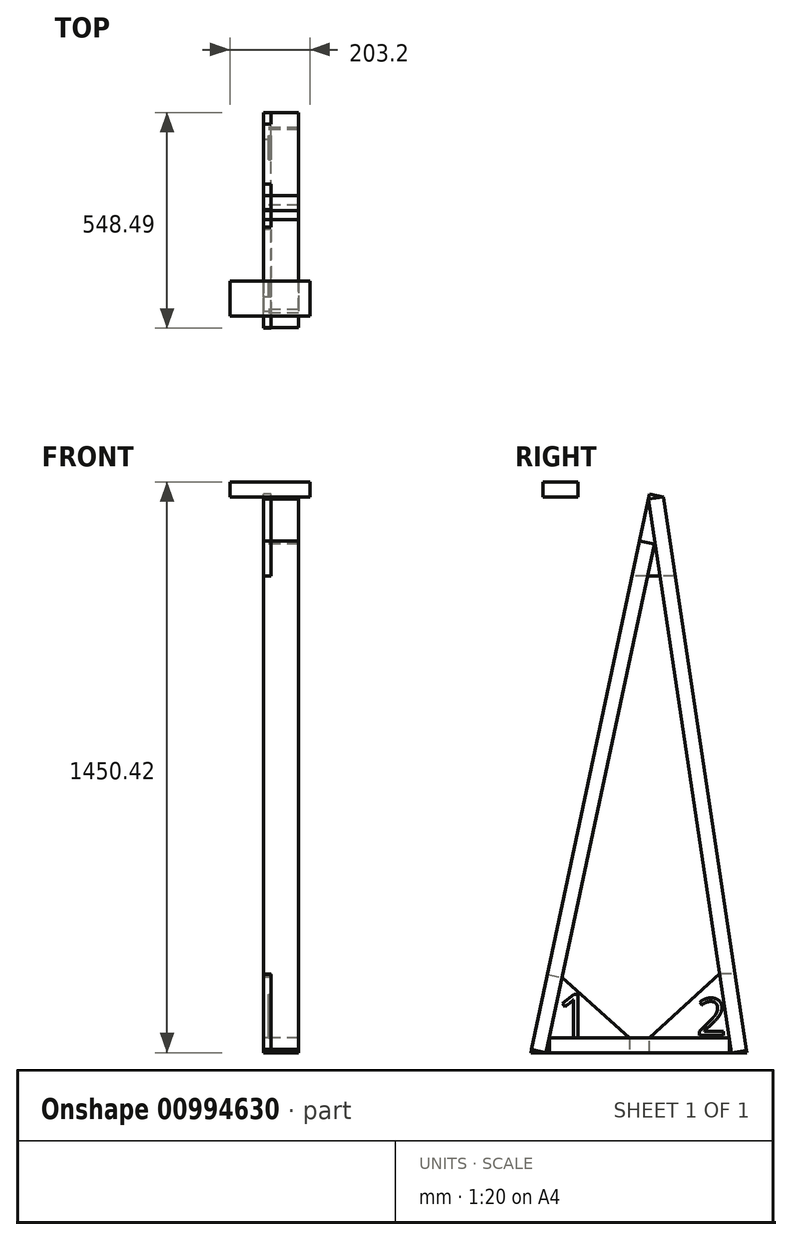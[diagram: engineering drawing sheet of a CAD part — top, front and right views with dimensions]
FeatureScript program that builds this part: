
annotation { "Feature Type Name" : "Feature", "Feature Type Description" : "" }
export const myFeature = defineFeature(function(context is Context, id is Id, definition is map)
    precondition{}
    {
        {
            var Q0;
            Q0=qCreatedBy(makeId("Right.planeOp"),FACE);
            var sketch = newSketch(context, id + "F0", { "sketchPlane" : qUnion([Q0])});
            skLineSegment(sketch, "E0.bottom", {"start": v(-72.85, 56) * mm, "end": v(384.35, 56) * mm});
            skLineSegment(sketch, "E0.top", {"start": v(-72.85, 17.9) * mm, "end": v(384.35, 17.9) * mm});
            skLineSegment(sketch, "E0.left", {"start": v(-72.85, 56) * mm, "end": v(-72.85, 17.9) * mm});
            skLineSegment(sketch, "E0.right", {"start": v(384.35, 56) * mm, "end": v(384.35, 17.9) * mm});
            skSolve(sketch);
        }
        {
            var Q0;
            Q0=makeQuery(id+"F0.imprint","IMPRINT",FACE,{"disambiguationData":[TD([[makeQuery(id+"F0.imprint","IMPRINT",EDGE,{"derivedFrom":sQuery(id+"F0.wireOp",EDGE,"E0.bottom")}),-1.0]])]});
            extrude(context, id + "F1", {"entities" : qUnion([Q0]), "depth" : 88.9 * mm, "offsetDistance" : 25.4 * mm});
        }
        {
            var Q0;
            Q0=qCreatedBy(makeId("Right.planeOp"),FACE);
            var sketch = newSketch(context, id + "F2", { "sketchPlane" : qUnion([Q0])});
            skLineSegment(sketch, "E1.bottom", {"start": v(156.4, 1317.77) * mm, "end": v(193.66, 1309.84) * mm});
            skLineSegment(sketch, "E1.top", {"start": v(-118.22, 25.83) * mm, "end": v(-80.95, 17.9) * mm});
            skLineSegment(sketch, "E1.left", {"start": v(156.4, 1317.77) * mm, "end": v(-118.22, 25.83) * mm});
            skLineSegment(sketch, "E1.right", {"start": v(193.66, 1309.84) * mm, "end": v(-80.95, 17.9) * mm});
            skSolve(sketch);
        }
        {
            var Q0;
            Q0=makeQuery(id+"F2.imprint","IMPRINT",FACE,{"disambiguationData":[TD([[makeQuery(id+"F2.imprint","IMPRINT",EDGE,{"derivedFrom":sQuery(id+"F2.wireOp",EDGE,"E1.bottom")}),-1.0]])]});
            extrude(context, id + "F3", {"entities" : qUnion([Q0]), "depth" : 88.9 * mm, "offsetDistance" : 25.4 * mm});
        }
        {
            var Q0;
            Q0=qCreatedBy(makeId("Right.planeOp"),FACE);
            var sketch = newSketch(context, id + "F4", { "sketchPlane" : qUnion([Q0])});
            skLineSegment(sketch, "E2.bottom", {"start": v(179.1, 1424.58) * mm, "end": v(216.77, 1430.23) * mm});
            skLineSegment(sketch, "E2.top", {"start": v(390.06, 17.9) * mm, "end": v(427.74, 23.56) * mm});
            skLineSegment(sketch, "E2.left", {"start": v(179.1, 1424.58) * mm, "end": v(390.06, 17.9) * mm});
            skLineSegment(sketch, "E2.right", {"start": v(216.77, 1430.23) * mm, "end": v(427.74, 23.56) * mm});
            skSolve(sketch);
        }
        {
            var Q0;
            Q0=makeQuery(id+"F4.imprint","IMPRINT",FACE,{"disambiguationData":[TD([[makeQuery(id+"F4.imprint","IMPRINT",EDGE,{"derivedFrom":sQuery(id+"F4.wireOp",EDGE,"E2.bottom")}),-1.0]])]});
            extrude(context, id + "F5", {"entities" : qUnion([Q0]), "depth" : 88.9 * mm, "offsetDistance" : 25.4 * mm});
        }
        {
            var Q0;
            Q0=qCreatedBy(makeId("Front.planeOp"),FACE);
            var sketch = newSketch(context, id + "F6", { "sketchPlane" : qUnion([Q0])});
            skLineSegment(sketch, "E3.bottom", {"start": v(-85.7, 1468.33) * mm, "end": v(117.5, 1468.33) * mm});
            skLineSegment(sketch, "E3.top", {"start": v(-85.7, 1430.23) * mm, "end": v(117.5, 1430.23) * mm});
            skLineSegment(sketch, "E3.left", {"start": v(-85.7, 1468.33) * mm, "end": v(-85.7, 1430.23) * mm});
            skLineSegment(sketch, "E3.right", {"start": v(117.5, 1468.33) * mm, "end": v(117.5, 1430.23) * mm});
            skSolve(sketch);
        }
        {
            var Q0;
            Q0=makeQuery(id+"F6.imprint","IMPRINT",FACE,{"disambiguationData":[TD([[makeQuery(id+"F6.imprint","IMPRINT",EDGE,{"derivedFrom":sQuery(id+"F6.wireOp",EDGE,"E3.bottom")}),-1.0]])]});
            extrude(context, id + "F7", {"entities" : qUnion([Q0]), "depth" : 88.9 * mm, "offsetDistance" : 25.4 * mm});
        }
        {
            var Q0;
            Q0=qCreatedBy(makeId("Right.planeOp"),FACE);
            var sketch = newSketch(context, id + "F8", { "sketchPlane" : qUnion([Q0])});
            skLineSegment(sketch, "E4", {"start": v(-119.9, 17.9) * mm, "end": v(-77.65, 216.67) * mm});
            skLineSegment(sketch, "E5", {"start": v(-77.65, 216.67) * mm, "end": v(-40.39, 208.75) * mm});
            skLineSegment(sketch, "E6", {"start": v(-40.39, 208.75) * mm, "end": v(130.35, 56) * mm});
            skLineSegment(sketch, "E7", {"start": v(130.35, 56) * mm, "end": v(130.35, 17.9) * mm});
            skLineSegment(sketch, "E8", {"start": v(130.35, 17.9) * mm, "end": v(-119.9, 17.9) * mm});
            skSolve(sketch);
        }
        {
            var Q0;
            Q0=qSketchRegion(id+"F8",true);
            extrude(context, id + "F9", {"entities" : qUnion([Q0]), "depth" : 19.05 * mm, "offsetDistance" : 25.4 * mm});
        }
        {
            var Q0;
            Q0=makeQuery(id+"F9.opExtrude","CAP_FACE",FACE,{"disambiguationData":[OSD([sQuery(id+"F8.wireOp",EDGE,"E4"),sQuery(id+"F8.wireOp",EDGE,"E5"),sQuery(id+"F8.wireOp",EDGE,"E6"),sQuery(id+"F8.wireOp",EDGE,"E7"),sQuery(id+"F8.wireOp",EDGE,"E8")])],"isStart":false});
            var sketch = newSketch(context, id + "F10", { "sketchPlane" : qUnion([Q0])});
            skText(sketch, "E9", { "text": "1", "fontName": "OpenSans-Regular.ttf"});
            const initialGuessF10  = {"E9": [-0.05357, 0.056, 1, 0, 0.11046]};
            skSetInitialGuess(sketch, initialGuessF10);
            skSolve(sketch);
        }
        {
            var Q0;
            Q0=qSketchRegion(id+"F10",true);
            extrude(context, id + "F11", {"entities" : qUnion([Q0]), "operationType" : NewBodyOperationType.REMOVE, "oppositeDirection" : true, "depth" : 6.35 * mm, "offsetDistance" : 25.4 * mm});
        }
        {
            var Q0;
            Q0=qCreatedBy(makeId("Right.planeOp"),FACE);
            var sketch = newSketch(context, id + "F12", { "sketchPlane" : qUnion([Q0])});
            skLineSegment(sketch, "E10", {"start": v(181.15, 17.9) * mm, "end": v(181.15, 56) * mm});
            skLineSegment(sketch, "E11", {"start": v(181.15, 56) * mm, "end": v(359.92, 218.86) * mm});
            skLineSegment(sketch, "E12", {"start": v(359.92, 218.86) * mm, "end": v(398.45, 218.86) * mm});
            skLineSegment(sketch, "E13", {"start": v(398.45, 218.86) * mm, "end": v(428.59, 17.9) * mm});
            skLineSegment(sketch, "E14", {"start": v(181.15, 17.9) * mm, "end": v(428.59, 17.9) * mm});
            skSolve(sketch);
        }
        {
            var Q0;
            Q0=makeQuery(id+"F12.imprint","IMPRINT",FACE,{"disambiguationData":[TD([[makeQuery(id+"F12.imprint","IMPRINT",EDGE,{"derivedFrom":sQuery(id+"F12.wireOp",EDGE,"E10")}),-1.0]])]});
            extrude(context, id + "F13", {"entities" : qUnion([Q0]), "depth" : 19.05 * mm, "offsetDistance" : 25.4 * mm});
        }
        {
            var Q0;
            Q0=makeQuery(id+"F13.opExtrude","CAP_FACE",FACE,{"disambiguationData":[OSD([sQuery(id+"F12.wireOp",EDGE,"E10"),sQuery(id+"F12.wireOp",EDGE,"E11"),sQuery(id+"F12.wireOp",EDGE,"E12"),sQuery(id+"F12.wireOp",EDGE,"E13"),sQuery(id+"F12.wireOp",EDGE,"E14")])],"isStart":false});
            var sketch = newSketch(context, id + "F14", { "sketchPlane" : qUnion([Q0])});
            skText(sketch, "E15", { "text": "2", "fontName": "OpenSans-Regular.ttf"});
            const initialGuessF14  = {"E15": [0.3018, 0.06236, 1, 0, 0.09411]};
            skSetInitialGuess(sketch, initialGuessF14);
            skSolve(sketch);
        }
        {
            var Q0;
            Q0=qSketchRegion(id+"F14",true);
            extrude(context, id + "F15", {"entities" : qUnion([Q0]), "operationType" : NewBodyOperationType.REMOVE, "oppositeDirection" : true, "depth" : 6.35 * mm, "offsetDistance" : 25.4 * mm});
        }
        {
            var Q0;
            Q0=qCreatedBy(makeId("Right.planeOp"),FACE);
            var sketch = newSketch(context, id + "F16", { "sketchPlane" : qUnion([Q0])});
            skLineSegment(sketch, "E16", {"start": v(137.58, 1229.27) * mm, "end": v(181.87, 1437.64) * mm});
            skLineSegment(sketch, "E17", {"start": v(181.87, 1437.64) * mm, "end": v(216.77, 1430.23) * mm});
            skLineSegment(sketch, "E18", {"start": v(216.77, 1430.23) * mm, "end": v(246.91, 1229.27) * mm});
            skLineSegment(sketch, "E19", {"start": v(246.91, 1229.27) * mm, "end": v(137.58, 1229.27) * mm});
            skSolve(sketch);
        }
        {
            var Q0;
            Q0=qSketchRegion(id+"F16",true);
            extrude(context, id + "F17", {"entities" : qUnion([Q0]), "depth" : 19.05 * mm, "offsetDistance" : 25.4 * mm});
        }
        {
            var Q0;
            Q0=makeQuery(id+"F17.opExtrude","CAP_FACE",FACE,{"disambiguationData":[OSD([sQuery(id+"F16.wireOp",EDGE,"E16"),sQuery(id+"F16.wireOp",EDGE,"E17"),sQuery(id+"F16.wireOp",EDGE,"E18"),sQuery(id+"F16.wireOp",EDGE,"E19")])],"isStart":false});
            var sketch = newSketch(context, id + "F18", { "sketchPlane" : qUnion([Q0])});
            skText(sketch, "E20", { "text": "3", "fontName": "OpenSans-Regular.ttf"});
            const initialGuessF18  = {"E20": [0.34625, 1.2752, 1, 0, 0.06328]};
            skSetInitialGuess(sketch, initialGuessF18);
            skSolve(sketch);
        }
        {
            var Q0;
            Q0=qSketchRegion(id+"F18",true);
            extrude(context, id + "F19", {"entities" : qUnion([Q0]), "operationType" : NewBodyOperationType.REMOVE, "oppositeDirection" : true, "depth" : 6.35 * mm, "offsetDistance" : 25.4 * mm});
        }
    });
